FCSTD DOCUMENT  (FreeCAD 0.18R16161 (Git))
Label: fixator01
License: All rights reserved
LicenseURL: http://en.wikipedia.org/wiki/All_rights_reserved
objects: Sketcher::SketchObject×1
note: 1 computed .brp shape members not serialized (recipe doc carries the construction recipe); baked Part::Feature solids carry a one-line shape summary decoded from their .brp

FEATURE [Sketcher::SketchObject] Sketch
  sketch-geometry (20):
    g0: LineSegment StartX=2.3094 StartY=4 StartZ=0 EndX=-2.3094 EndY=4 EndZ=0
    g1: LineSegment StartX=-2.3094 StartY=4 StartZ=0 EndX=0 EndY=0 EndZ=0
    g2: LineSegment StartX=0 StartY=0 StartZ=0 EndX=2.3094 EndY=4 EndZ=0
    g3: Circle [constr] CenterX=0 CenterY=2.66667 CenterZ=0 NormalX=0 NormalY=0 NormalZ=1 AngleXU=0 Radius=2.66667
    g4: LineSegment StartX=2.3094 StartY=-4 StartZ=0 EndX=0 EndY=0 EndZ=0
    g5: LineSegment StartX=0 StartY=0 StartZ=0 EndX=-2.3094 EndY=-4 EndZ=0
    g6: LineSegment StartX=-2.3094 StartY=-4 StartZ=0 EndX=2.3094 EndY=-4 EndZ=0
    g7: Circle [constr] CenterX=0 CenterY=-2.66667 CenterZ=0 NormalX=0 NormalY=0 NormalZ=1 AngleXU=0 Radius=2.66667
    g8: LineSegment StartX=2.3094 StartY=4 StartZ=0 EndX=6.3094 EndY=4 EndZ=0
    g9: LineSegment StartX=2.3094 StartY=-4 StartZ=0 EndX=6.3094 EndY=-4 EndZ=0
    g10: LineSegment StartX=6.3094 StartY=4 StartZ=0 EndX=6.3094 EndY=-4 EndZ=0
    g11: LineSegment StartX=6.3094 StartY=4 StartZ=0 EndX=8.6188 EndY=0 EndZ=0
    g12: LineSegment StartX=6.3094 StartY=-4 StartZ=0 EndX=8.6188 EndY=0 EndZ=0
    g13: LineSegment StartX=-2.3094 StartY=4 StartZ=0 EndX=-6.3094 EndY=4 EndZ=0
    g14: LineSegment StartX=-2.3094 StartY=-4 StartZ=0 EndX=-6.3094 EndY=-4 EndZ=0
    g15: LineSegment StartX=-6.3094 StartY=4 StartZ=0 EndX=-6.3094 EndY=-4 EndZ=0
    g16: LineSegment StartX=-6.3094 StartY=4 StartZ=0 EndX=-8.6188 EndY=0 EndZ=0
    g17: LineSegment StartX=-8.6188 StartY=0 StartZ=0 EndX=-6.3094 EndY=-4 EndZ=0
    g18: ArcOfCircle CenterX=9.2376 CenterY=4e-16 CenterZ=0 NormalX=0 NormalY=0 NormalZ=1 AngleXU=0 Radius=8 StartAngle=2.61799 EndAngle=3.66519
    g19: ArcOfCircle CenterX=-9.2376 CenterY=-2e-16 CenterZ=0 NormalX=0 NormalY=0 NormalZ=1 AngleXU=0 Radius=8 StartAngle=5.75959 EndAngle=6.80678
  constraints (54):
    c: Coincident(g0,g1)
    c: Coincident(g1,g2)
    c: Coincident(g2,g0)
    c: Equal(g0,g1)
    c: Equal(g0,g2)
    c: PointOnObject(g0,g3)
    c: PointOnObject(g1,g3)
    c: PointOnObject(g2,g3)
    c: PointOnObject(g3,g-2)
    c: Coincident(g1,g-1)
    c: Coincident(g4,g5)
    c: Coincident(g5,g6)
    c: Coincident(g6,g4)
    c: Equal(g4,g5)
    c: Equal(g4,g6)
    c: PointOnObject(g4,g7)
    c: PointOnObject(g5,g7)
    c: PointOnObject(g6,g7)
    c: PointOnObject(g7,g-2)
    c: Coincident(g4,g1)
    c: Equal(g6,g0)
    c: Horizontal(g8)
    c: Coincident(g8,g0)
    c: DistanceX(g8,g8) = 4
    c: Horizontal(g9)
    c: Coincident(g9,g4)
    c: Equal(g9,g8)
    c: Coincident(g10,g8)
    c: Coincident(g10,g9)
    c: Coincident(g11,g8)
    c: Coincident(g12,g9)
    c: PointOnObject(g11,g-1)
    c: Coincident(g12,g11)
    c: DistanceY(g9,g8) = 8
    c: Equal(g11,g2)
    c: Coincident(g13,g0)
    c: Coincident(g14,g5)
    c: Horizontal(g13)
    c: Horizontal(g14)
    c: Coincident(g15,g13)
    c: Coincident(g15,g14)
    c: Equal(g8,g13)
    c: Equal(g14,g13)
    c: Coincident(g16,g13)
    c: Coincident(g17,g14)
    c: PointOnObject(g16,g-1)
    c: Coincident(g17,g16)
    c: Equal(g16,g0)
    c: Coincident(g18,g0)
    c: Coincident(g18,g4)
    c: Radius(g18) = 8
    c: Coincident(g19,g0)
    c: Coincident(g19,g5)
    c: Equal(g19,g18)
